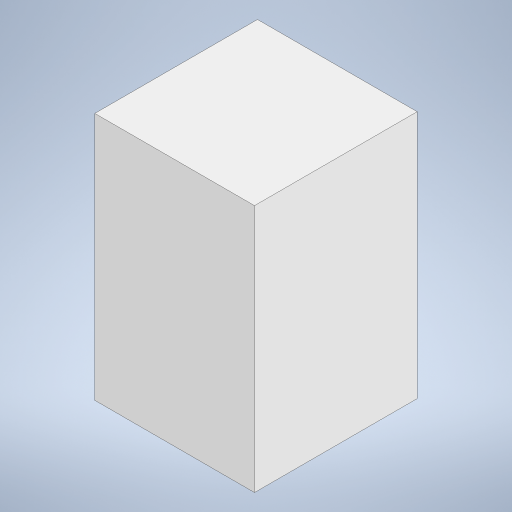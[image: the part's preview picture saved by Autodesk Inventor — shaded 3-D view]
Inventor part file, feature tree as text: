
AUTODESK INVENTOR PART (.ipt)
format: ipt  version: 2024 (Build 280153000, 153)  size: 175,616 bytes
history: native  units: in
note: dims shown in document units (in); Inventor stores cm internally (conversion verified against a paired STEP export)
features: extrude x1, sketch x1
ambient origin geometry x8: Origin, YZ Plane, XZ Plane, XY Plane, X Axis, Y Axis, Z Axis, Center Point
bodies: Solid1 (feature_tree)
feature tree (2):
  extrude  "Extrusion1"  Depth=42.0in
  sketch  "Sketch1"  dims[d2=27.5in d3=42.0in d4=27.0in d5=0.0in]
